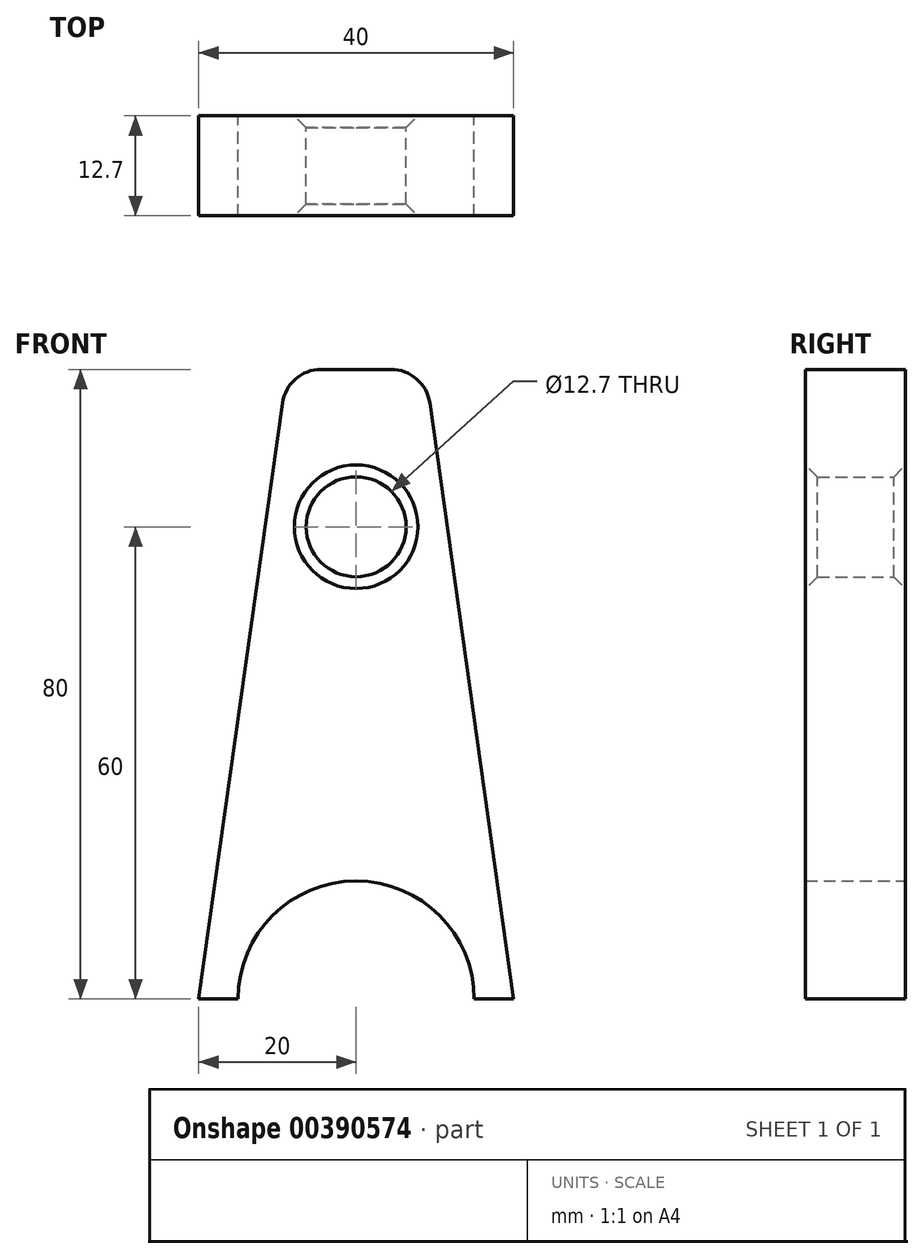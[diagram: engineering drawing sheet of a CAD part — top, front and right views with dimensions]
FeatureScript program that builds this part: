
annotation { "Feature Type Name" : "Feature", "Feature Type Description" : "" }
export const myFeature = defineFeature(function(context is Context, id is Id, definition is map)
    precondition{}
    {
        {
            var Q0;
            Q0=qCreatedBy(makeId("Front.planeOp"),FACE);
            var sketch = newSketch(context, id + "F0", { "sketchPlane" : qUnion([Q0])});
            skLineSegment(sketch, "E0", {"start": v(20, 0) * mm, "end": v(-20, 0) * mm, "construction": true});
            skLineSegment(sketch, "E1", {"start": v(9.36, 75.7) * mm, "end": v(20, 0) * mm});
            skArc(sketch, "E2", {"start": v(15, 0) * mm, "mid": v(0, 15) * mm, "end": v(-15, 0) * mm});
            skLineSegment(sketch, "E3", {"start": v(-20, 0) * mm, "end": v(-15, 0) * mm});
            skLineSegment(sketch, "E4", {"start": v(15, 0) * mm, "end": v(20, 0) * mm});
            skLineSegment(sketch, "E5", {"start": v(20, 0) * mm, "end": v(20, 71.07) * mm, "construction": true});
            skLineSegment(sketch, "E6", {"start": v(-20, 0) * mm, "end": v(-20, 70.52) * mm, "construction": true});
            skLineSegment(sketch, "E7", {"start": v(-20, 0) * mm, "end": v(-9.36, 75.7) * mm});
            skLineSegment(sketch, "E8", {"start": v(-4.41, 80) * mm, "end": v(4.41, 80) * mm});
            skPoint(sketch, "E9.orphan", {"position": v(0, 142.3) * mm});
            skLineSegment(sketch, "E10", {"start": v(0, 0) * mm, "end": v(0, 80) * mm, "construction": true});
            skCircle(sketch, "E11", {"center": v(0, 60) * mm, "radius": 6.35 * mm});
            skPoint(sketch, "E12.visualSharp", {"position": v(-8.76, 80) * mm});
            skArc(sketch, "E12.filletArc", {"start": v(-4.41, 80) * mm, "mid": v(-7.7, 78.77) * mm, "end": v(-9.36, 75.7) * mm});
            skPoint(sketch, "E13.visualSharp", {"position": v(8.76, 80) * mm});
            skArc(sketch, "E13.filletArc", {"start": v(9.36, 75.7) * mm, "mid": v(7.7, 78.77) * mm, "end": v(4.41, 80) * mm});
            skSolve(sketch);
        }
        {
            var Q0;
            Q0 = qSketchRegion(id + "F0", true);
            extrude(context, id + "F1", {"entities" : qUnion([Q0]), "depth" : 12.7 * mm});
        }
        {
            var Q0;
            Q0=makeQuery(id+"F1.opExtrude","CAP_EDGE",EDGE,{"disambiguationData":[OSD([sQuery(id+"F0.wireOp",EDGE,"E11")])],"isStart":false});
            var Q1;
            Q1=makeQuery(id+"F1.opExtrude","CAP_EDGE",EDGE,{"disambiguationData":[OSD([sQuery(id+"F0.wireOp",EDGE,"E11")])],"isStart":true});
            chamfer(context, id + "F2", {"entities" : qUnion([Q0, Q1]), "width" : 1.5 * mm, "tangentPropagation" : true});
        }
    });
